# Revit family: Deca_Bacia Sanitária Convencional Piano_P.33
name_source: partatom
category: Plumbing Fixtures
revit_build: Autodesk Revit Architecture 2012 (Build: 20110916_2132(x64)
units: mm (PartAtom-declared; Revit-internal decimal feet)

## types (2) — shared parameters
Aprovado por = Contino/quattroD
Assembly Code = D2010110
Atendimento ao Cliente = 0800-0117073
Consumo = 6 lpf
Criado por = Contino/quattroD
Description = Bacia sanitária convencional
Diâmetro Ponto de Esgoto = 100 mm  [stored 0.328084 ft]
Diâmetro Água Fria = 40 mm  [stored 0.131234 ft]
Flow Pressure = 0.00 psi
Linha = Piano
Louça/Metais = Louça
Manufacturer = Deca
Material = Deca_Vitreous China
Norma = ABNT NBR 15097-1: 2011
Peso Liquido (Kg) = 28.3
Pressão = 2 a 40 mca
Produto = Bacia sanitária convencional Piano
Raio Ponto de Esgoto = 50 mm  [stored 0.164042 ft]
Raio Água Fria = 20 mm  [stored 0.0656168 ft]
Segmento = Luxo
URL = www.deca.com.br/produtos
Variações de COR = Branco (P.33.17); Ébano (P.33.95).
Vendido Separadamente = Kit de instalação bacia convencional fixação lateral (1201.C.KIT.P) ou Anel de vedação (AV.90.01 ).  Tubo de ligação com anel expansor: Cromado (1968.C), Branco (1968.E.BR), Dourado (1968.D), Gold (1968.D.GDL).  Parafuso de fixação: Cromado (SP.121.01) , Dourado (SP.121.03) e Gold (SP.121.GLD.03).  Assentos Compatíveis: Assento termofixo slow close:  Branco (AP.336.17), Ébano (AP.336.95).  Assento Poliéster - Fixação Cromada: Branco (AP.33.17), Ébano (AP.33.95). Assento Poliéster - Fixação Dourada: Branco(AP.330.17), Ébano (AP.330.95). Assento poliéster slow close: Branco (AP337.17); Ébano (AP337.95).
zero-valued in all types: CWFU, Default Elevation, WFU

## per-type parameters (varying)
| type | Bacia | Código | Model |
| P.33.17_Branco Gelo GE17 | Deca GE17 Branco Gelo Cerâmica | P.33.17 | P.33.17 |
| P.33.95_Ébano EB95 | Deca EB95 Ébano Cerâmica | P.33.95 | P.33.95 |

note: [stored X ft] marks values corroborated as IEEE doubles in the binary element streams (Revit-internal decimal feet)

## geometry (parser evidence)
native form markers: Blend x8, Sweep x4
no freeform markers — native parametric forms only
